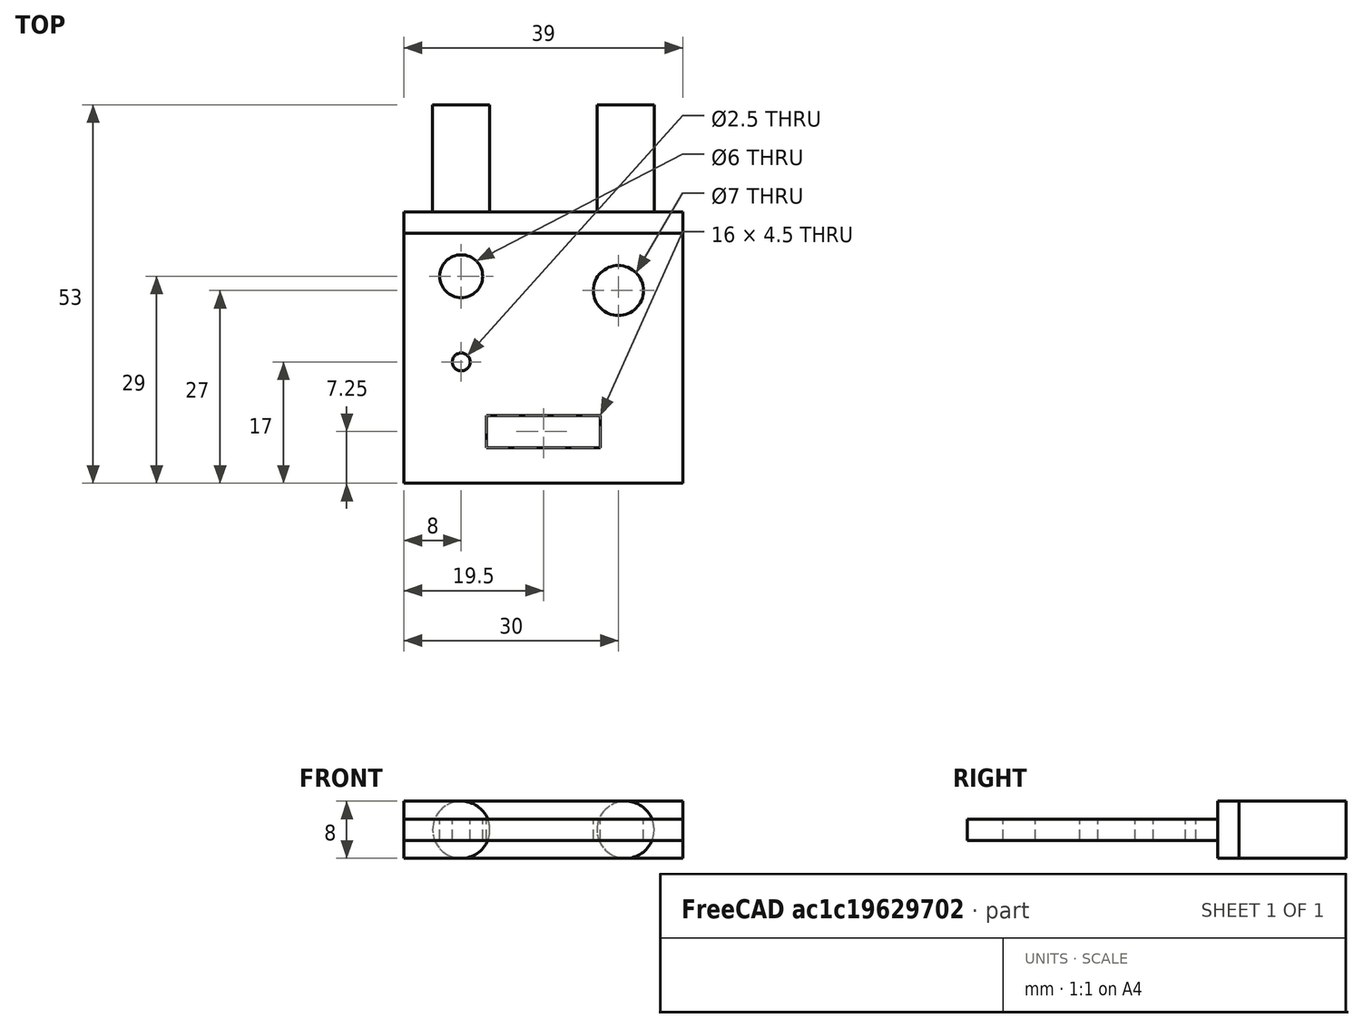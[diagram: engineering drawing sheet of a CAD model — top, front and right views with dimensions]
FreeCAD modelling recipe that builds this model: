
FCSTD DOCUMENT  (FreeCAD 0.15R4671 (Git))
Label: Holder_V8
License: All rights reserved
LicenseURL: http://en.wikipedia.org/wiki/All_rights_reserved
objects: Part::Cylinder×5, Part::Box×3, Part::MultiFuse×1, Part::Cut×1
note: 10 computed .brp shape members not serialized (recipe doc carries the construction recipe); baked Part::Feature solids carry a one-line shape summary decoded from their .brp

FEATURE [Part::Box] Box  label="Base"
  Height = 8
  Length = 39
  Placement = pos=(-8,-18,-4) rot=(0,0,1;0rad)
  Width = 3
FEATURE [Part::Cylinder] Cylinder  label="Pin2"
  Angle = 360
  Height = 15
  Placement = pos=(23,0,0) rot=(1,0,0;1.5708rad)
  Radius = 4
FEATURE [Part::Cylinder] Cylinder001  label="Pin1"
  Angle = 360
  Height = 15
  Placement = pos=(0,0,0) rot=(1,0,0;1.5708rad)
  Radius = 4
FEATURE [Part::Box] Box001  label="Holder"
  Height = 3
  Length = 39
  Placement = pos=(-8,-53,-1.5) rot=(0,0,1;0rad)
  Width = 35
FEATURE [Part::Cylinder] Cylinder002  label="Cut1"
  Angle = 360
  Height = 3
  Placement = pos=(22,-26,-1.5) rot=(0,0,1;0rad)
  Radius = 3.5
FEATURE [Part::Cylinder] Cylinder003  label="Cut2"
  Angle = 360
  Height = 3
  Placement = pos=(0,-24,-1.5) rot=(0,0,1;0rad)
  Radius = 3
FEATURE [Part::Cylinder] Cylinder004  label="Cut3"
  Angle = 360
  Height = 3
  Placement = pos=(0,-36,-1.5) rot=(0,0,1;0rad)
  Radius = 1.25
FEATURE [Part::Box] Box002  label="Cut4"
  Height = 3
  Length = 16
  Placement = pos=(3.5,-48,-1.5) rot=(0,0,1;0rad)
  Width = 4.5
FEATURE [Part::MultiFuse] Fusion  label="cuts"
  Shapes = -> [Cylinder004,Cylinder003,Cylinder002,Box002]
FEATURE [Part::Cut] Cut
  Base = -> Box001
  Tool = -> Fusion
